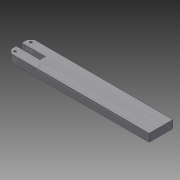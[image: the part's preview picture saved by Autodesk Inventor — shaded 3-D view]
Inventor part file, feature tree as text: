
AUTODESK INVENTOR PART (.ipt)
format: ipt  version: 2015 (Build 190159000, 159)  size: 117,248 bytes
history: native  units: mm
features: sketch x4, extrude x3, hole x1, chamfer x1
ambient origin geometry x8: Origin, YZ Plane, XZ Plane, XY Plane, X Axis, Y Axis, Z Axis, Center Point
bodies: Solid1 (feature_tree)
feature tree (9):
  extrude  "Extrusion1"  Depth=30.0mm
  hole  "Hole1"  [1 undecoded]
  chamfer  "Chamfer1"  Distance=5.0mm
  extrude  "Extrusion2"  Depth=4.0mm TaperAngle=45.0deg
  extrude  "Extrusion3"  Depth=4.0mm
  sketch  "Sketch1"  dims[d0=180.0mm d1=30.0mm]
  sketch  "Sketch2"  dims[d2=10.0mm d3=0.0mm d4=5.0mm]
  sketch  "Sketch3"  dims[d5=5.0mm]
  sketch  "Sketch4"  dims[d6=5.0mm d7=5.0mm d8=3.0mm d9=6.0mm d10=4.0mm d11=2.0mm d12=90.0deg d13=10.0mm d14=20.594885mm d15=5.0mm d16=2.0mm d17=45.0deg d18=5.0mm d19=5.0mm d20=30.0mm d21=10.0mm d22=0.0mm d23=8.0mm d24=8.0mm d25=30.0mm d26=4.0mm d27=0.0mm]
note: 1 required parameter value undecoded (feature->parameter linkage not recoverable at this tier; creation-order binding heuristic only, values carry confidence <= 0.55)
